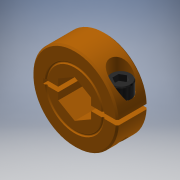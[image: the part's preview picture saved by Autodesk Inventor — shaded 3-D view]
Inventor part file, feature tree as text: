
AUTODESK INVENTOR PART (.ipt)
format: ipt  version: 2017.1 (Build 211199000, 199)  size: 302,080 bytes
history: native  units: in
note: dims shown in document units (in); Inventor stores cm internally (conversion verified against a paired STEP export)
features: extrude x2, sketch x2, other x1, imported_body x1
ambient origin geometry x8: Origin, YZ Plane, XZ Plane, XY Plane, X Axis, Y Axis, Z Axis, Center Point
bodies: Solid1 (feature_tree)
feature tree (6):
  other  "CL-8-A1"
  extrude  "Extrusion1"  Depth=0.4375in TaperAngle=0.0deg
  extrude  "Extrusion2"  [1 undecoded]
  imported_body  "Base1"
  sketch  "Sketch2"  dims[d0=0.5in d1=0.4375in d2=0.0in]
  sketch  "Sketch3"  dims[d3=1.0in d4=0.0in]
note: 1 required parameter value undecoded (feature->parameter linkage not recoverable at this tier; creation-order binding heuristic only, values carry confidence <= 0.55)
